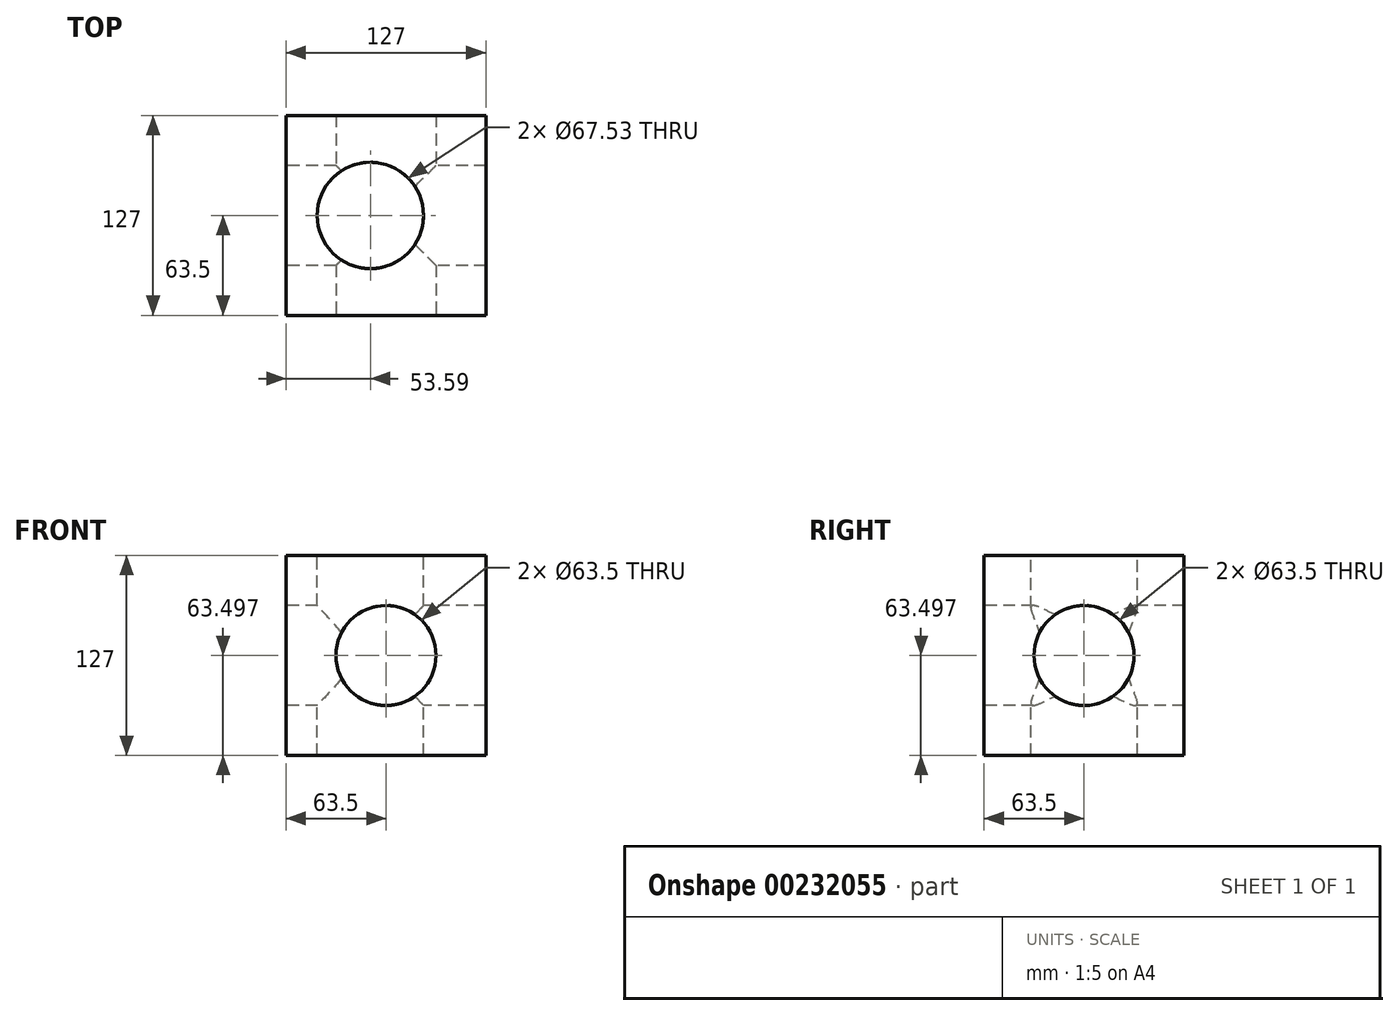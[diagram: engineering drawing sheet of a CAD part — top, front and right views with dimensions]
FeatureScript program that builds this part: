
annotation { "Feature Type Name" : "Feature", "Feature Type Description" : "" }
export const myFeature = defineFeature(function(context is Context, id is Id, definition is map)
    precondition{}
    {
        {
            var Q0;
            Q0=qCreatedBy(makeId("Front.planeOp"),FACE);
            var sketch = newSketch(context, id + "F4", { "sketchPlane" : qUnion([Q0])});
            skLineSegment(sketch, "E0.bottom", {"start": v(73.4, 104.2) * mm, "end": v(-53.6, 104.2) * mm});
            skLineSegment(sketch, "E0.top", {"start": v(73.4, -22.8) * mm, "end": v(-53.6, -22.8) * mm});
            skLineSegment(sketch, "E0.left", {"start": v(73.4, 104.2) * mm, "end": v(73.4, -22.8) * mm});
            skLineSegment(sketch, "E0.right", {"start": v(-53.6, 104.2) * mm, "end": v(-53.6, -22.8) * mm});
            skPoint(sketch, "E0.middle", {"position": v(9.9, 40.7) * mm});
            skSolve(sketch);
        }
        {
            var Q0;
            Q0 = qSketchRegion(id + "F4", true);
            extrude(context, id + "F5", {"entities" : qUnion([Q0]), "depth" : 127 * mm});
        }
        {
            var Q0;
            Q0=makeQuery(id+"F5.opExtrude","SWEPT_FACE",FACE,{"disambiguationData":[OSD([sQuery(id+"F4.wireOp",EDGE,"E0.bottom")])]});
            var sketch = newSketch(context, id + "F0", { "sketchPlane" : qUnion([Q0])});
            skCircle(sketch, "E1", {"center": v(0, -63.5) * mm, "radius": 33.77 * mm});
            skPoint(sketch, "E1.centerSnap0", {"position": v(73.4, -63.5) * mm});
            skSolve(sketch);
        }
        {
            var Q0;
            Q0=makeQuery(id+"F0.imprint","IMPRINT",FACE,{"disambiguationData":[TD([[makeQuery(id+"F0.imprint","IMPRINT",EDGE,{"derivedFrom":sQuery(id+"F0.wireOp",EDGE,"E1")}),1.0]])]});
            extrude(context, id + "F1", {"entities" : qUnion([Q0]), "operationType" : NewBodyOperationType.REMOVE, "oppositeDirection" : true, "depth" : 193.62 * mm});
        }
        {
            var Q0;
            Q0=makeQuery(id+"F5.opExtrude","CAP_FACE",FACE,{"disambiguationData":[OSD([sQuery(id+"F4.wireOp",EDGE,"E0.bottom"),sQuery(id+"F4.wireOp",EDGE,"E0.top"),sQuery(id+"F4.wireOp",EDGE,"E0.left"),sQuery(id+"F4.wireOp",EDGE,"E0.right")])],"isStart":false});
            var sketch = newSketch(context, id + "F2", { "sketchPlane" : qUnion([Q0])});
            skCircle(sketch, "E2", {"center": v(9.9, 40.7) * mm, "radius": 31.75 * mm});
            skPoint(sketch, "E2.centerSnap0", {"position": v(9.9, 104.2) * mm});
            skPoint(sketch, "E2.centerSnap1", {"position": v(-53.6, 40.7) * mm});
            skSolve(sketch);
        }
        {
            var Q0;
            Q0=makeQuery(id+"F2.imprint","IMPRINT",FACE,{"disambiguationData":[TD([[makeQuery(id+"F2.imprint","IMPRINT",EDGE,{"derivedFrom":sQuery(id+"F2.wireOp",EDGE,"E2")}),1.0]])]});
            extrude(context, id + "F6", {"entities" : qUnion([Q0]), "operationType" : NewBodyOperationType.REMOVE, "oppositeDirection" : true, "depth" : 333.53 * mm});
        }
        {
            var Q0;
            Q0=makeQuery(id+"F5.opExtrude","SWEPT_FACE",FACE,{"disambiguationData":[OSD([sQuery(id+"F4.wireOp",EDGE,"E0.right")])]});
            var sketch = newSketch(context, id + "F3", { "sketchPlane" : qUnion([Q0])});
            skCircle(sketch, "E3", {"center": v(63.5, 40.7) * mm, "radius": 31.75 * mm});
            skPoint(sketch, "E3.centerSnap0", {"position": v(0, 40.7) * mm});
            skPoint(sketch, "E3.centerSnap1", {"position": v(63.5, -22.8) * mm});
            skSolve(sketch);
        }
        {
            var Q0;
            Q0=makeQuery(id+"F3.imprint","IMPRINT",FACE,{"disambiguationData":[TD([[makeQuery(id+"F3.imprint","IMPRINT",EDGE,{"derivedFrom":sQuery(id+"F3.wireOp",EDGE,"E3")}),1.0]])]});
            extrude(context, id + "F7", {"entities" : qUnion([Q0]), "operationType" : NewBodyOperationType.REMOVE, "oppositeDirection" : true, "depth" : 161.24 * mm});
        }
    });
